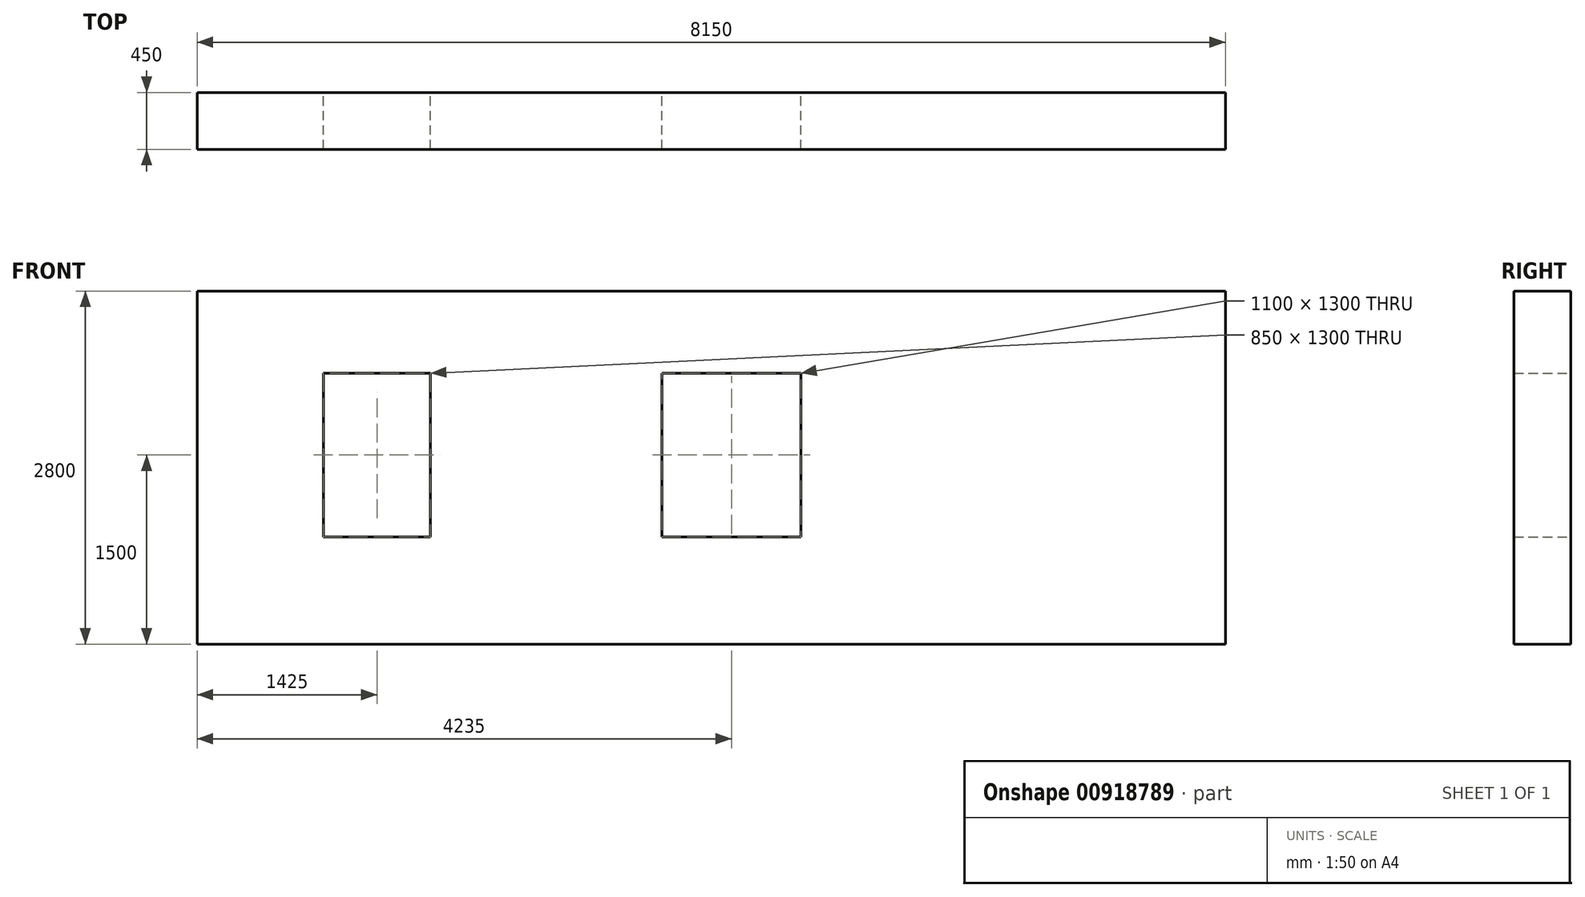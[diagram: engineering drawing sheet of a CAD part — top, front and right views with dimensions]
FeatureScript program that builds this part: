
annotation { "Feature Type Name" : "Feature", "Feature Type Description" : "" }
export const myFeature = defineFeature(function(context is Context, id is Id, definition is map)
    precondition{}
    {
        {
            var Q0;
            Q0=qCreatedBy(makeId("Front.planeOp"),FACE);
            var sketch = newSketch(context, id + "F0", { "sketchPlane" : qUnion([Q0])});
            skLineSegment(sketch, "E0.bottom", {"start": v(0, 0) * mm, "end": v(8150, 0) * mm});
            skLineSegment(sketch, "E0.top", {"start": v(0, 2800) * mm, "end": v(8150, 2800) * mm});
            skLineSegment(sketch, "E0.left", {"start": v(0, 0) * mm, "end": v(0, 2800) * mm});
            skLineSegment(sketch, "E0.right", {"start": v(8150, 0) * mm, "end": v(8150, 2800) * mm});
            skLineSegment(sketch, "E1.bottom", {"start": v(3685, 2150) * mm, "end": v(4785, 2150) * mm});
            skLineSegment(sketch, "E1.top", {"start": v(3685, 850) * mm, "end": v(4785, 850) * mm});
            skLineSegment(sketch, "E1.left", {"start": v(3685, 2150) * mm, "end": v(3685, 850) * mm});
            skLineSegment(sketch, "E1.right", {"start": v(4785, 2150) * mm, "end": v(4785, 850) * mm});
            skLineSegment(sketch, "E2.bottom", {"start": v(1000, 2150) * mm, "end": v(1850, 2150) * mm});
            skLineSegment(sketch, "E2.top", {"start": v(1000, 850) * mm, "end": v(1850, 850) * mm});
            skLineSegment(sketch, "E2.left", {"start": v(1000, 2150) * mm, "end": v(1000, 850) * mm});
            skLineSegment(sketch, "E2.right", {"start": v(1850, 2150) * mm, "end": v(1850, 850) * mm});
            skLineSegment(sketch, "E3", {"start": v(1850, 2150) * mm, "end": v(3685, 2150) * mm, "construction": true});
            skSolve(sketch);
        }
        {
            var Q0;
            Q0=makeQuery(id+"F0.imprint","IMPRINT",FACE,{"disambiguationData":[TD([[makeQuery(id+"F0.imprint","IMPRINT",EDGE,{"derivedFrom":sQuery(id+"F0.wireOp",EDGE,"E0.bottom")}),1.0]])]});
            extrude(context, id + "F1", {"entities" : qUnion([Q0]), "depth" : 450 * mm, "offsetDistance" : 25 * mm});
        }
    });
